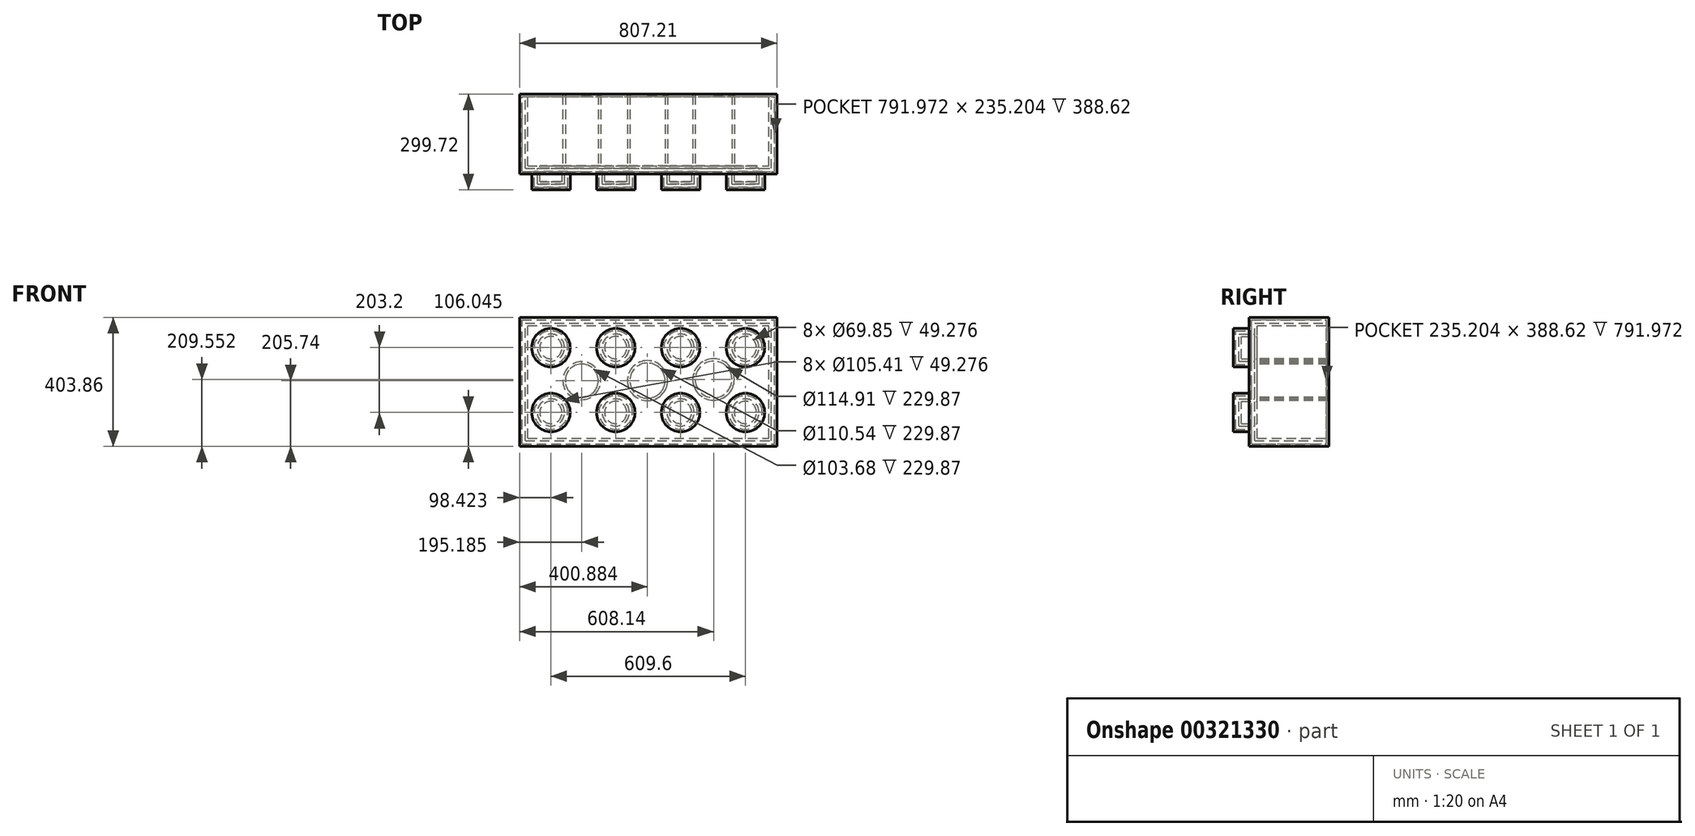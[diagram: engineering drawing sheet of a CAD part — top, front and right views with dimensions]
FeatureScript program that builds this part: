
annotation { "Feature Type Name" : "Feature", "Feature Type Description" : "" }
export const myFeature = defineFeature(function(context is Context, id is Id, definition is map)
    precondition{}
    {
        {
            var Q0;
            Q0=qCreatedBy(makeId("Front.planeOp"),FACE);
            var sketch = newSketch(context, id + "F0", { "sketchPlane" : qUnion([Q0])});
            skLineSegment(sketch, "E0.bottom", {"start": v(-361.72, 0) * mm, "end": v(445.49, 0) * mm});
            skLineSegment(sketch, "E0.top", {"start": v(-361.72, 403.86) * mm, "end": v(445.49, 403.86) * mm});
            skLineSegment(sketch, "E0.left", {"start": v(-361.72, 0) * mm, "end": v(-361.72, 403.86) * mm});
            skLineSegment(sketch, "E0.right", {"start": v(445.49, 0) * mm, "end": v(445.49, 403.86) * mm});
            skLineSegment(sketch, "E1.left", {"start": v(445.49, 0) * mm, "end": v(445.49, 0) * mm});
            skSolve(sketch);
        }
        {
            var Q0;
            Q0=makeQuery(id+"F0.imprint","IMPRINT",FACE,{"disambiguationData":[TD([[makeQuery(id+"F0.imprint","IMPRINT",EDGE,{"derivedFrom":sQuery(id+"F0.wireOp",EDGE,"E0.bottom")}),1.0]])]});
            extrude(context, id + "F1", {"entities" : qUnion([Q0]), "depth" : 250.44 * mm});
        }
        {
            var Q0;
            Q0=makeQuery(id+"F1.opExtrude","CAP_FACE",FACE,{"disambiguationData":[OSD([sQuery(id+"F0.wireOp",EDGE,"E0.bottom"),sQuery(id+"F0.wireOp",EDGE,"E0.top"),sQuery(id+"F0.wireOp",EDGE,"E0.left"),sQuery(id+"F0.wireOp",EDGE,"E0.right")])],"isStart":false});
            var sketch = newSketch(context, id + "F2", { "sketchPlane" : qUnion([Q0])});
            skCircle(sketch, "E2", {"center": v(-263.3, 309.25) * mm, "radius": 60.33 * mm});
            skCircle(sketch, "E3.0.1.0", {"center": v(-263.3, 106.05) * mm, "radius": 60.33 * mm});
            skCircle(sketch, "E3.1.0.0", {"center": v(-60.1, 309.25) * mm, "radius": 60.33 * mm});
            skCircle(sketch, "E3.1.1.0", {"center": v(-60.1, 106.05) * mm, "radius": 60.33 * mm});
            skCircle(sketch, "E3.2.0.0", {"center": v(143.1, 309.25) * mm, "radius": 60.33 * mm});
            skCircle(sketch, "E3.2.1.0", {"center": v(143.1, 106.05) * mm, "radius": 60.33 * mm});
            skCircle(sketch, "E3.3.0.0", {"center": v(346.3, 309.25) * mm, "radius": 60.33 * mm});
            skCircle(sketch, "E3.3.1.0", {"center": v(346.3, 106.05) * mm, "radius": 60.33 * mm});
            skLineSegment(sketch, "E3.direction1", {"start": v(-263.3, 309.25) * mm, "end": v(-60.1, 309.25) * mm, "construction": true});
            skLineSegment(sketch, "E3.direction2", {"start": v(-263.3, 309.25) * mm, "end": v(-263.3, 106.05) * mm, "construction": true});
            skSolve(sketch);
        }
        {
            var Q0;
            Q0 = qSketchRegion(id + "F2", true);
            extrude(context, id + "F3", {"entities" : qUnion([Q0]), "operationType" : NewBodyOperationType.ADD, "depth" : 49.28 * mm});
        }
        {
            var Q0;
            Q0=makeQuery(id+"F1.opExtrude","CAP_FACE",FACE,{"disambiguationData":[OSD([sQuery(id+"F0.wireOp",EDGE,"E0.bottom"),sQuery(id+"F0.wireOp",EDGE,"E0.top"),sQuery(id+"F0.wireOp",EDGE,"E0.left"),sQuery(id+"F0.wireOp",EDGE,"E0.right")])],"isStart":true});
            shell(context, id + "F4", {"entities" : qUnion([Q0]), "thickness" : 25.4 * mm});
        }
        {
            var Q0;
            Q0=makeQuery(id+"F4.opShell","OFFSET_FACE",FACE,{"disambiguationData":[OSD([sQuery(id+"F0.wireOp",EDGE,"E0.bottom"),sQuery(id+"F0.wireOp",EDGE,"E0.top"),sQuery(id+"F0.wireOp",EDGE,"E0.left"),sQuery(id+"F0.wireOp",EDGE,"E0.right")])]});
            var sketch = newSketch(context, id + "F5", { "sketchPlane" : qUnion([Q0])});
            skCircle(sketch, "E4", {"center": v(-246.42, 209.55) * mm, "radius": 65.08 * mm});
            skSolve(sketch);
        }
        {
            var Q0;
            Q0=makeQuery(id+"F5.imprint","IMPRINT",FACE,{"disambiguationData":[TD([[makeQuery(id+"F5.imprint","IMPRINT",EDGE,{"derivedFrom":sQuery(id+"F5.wireOp",EDGE,"E4")}),1.0]])]});
            extrude(context, id + "F6", {"entities" : qUnion([Q0]), "operationType" : NewBodyOperationType.ADD, "depth" : 222.25 * mm});
        }
        {
            var Q0;
            Q0=makeQuery(id+"F4.opShell","OFFSET_FACE",FACE,{"disambiguationData":[OSD([sQuery(id+"F0.wireOp",EDGE,"E0.bottom"),sQuery(id+"F0.wireOp",EDGE,"E0.top"),sQuery(id+"F0.wireOp",EDGE,"E0.left"),sQuery(id+"F0.wireOp",EDGE,"E0.right")])]});
            var sketch = newSketch(context, id + "F7", { "sketchPlane" : qUnion([Q0])});
            skCircle(sketch, "E5", {"center": v(-39.16, 205.74) * mm, "radius": 62.89 * mm});
            skSolve(sketch);
        }
        {
            var Q0;
            Q0=makeQuery(id+"F7.imprint","IMPRINT",FACE,{"disambiguationData":[TD([[makeQuery(id+"F7.imprint","IMPRINT",EDGE,{"derivedFrom":sQuery(id+"F7.wireOp",EDGE,"E5")}),1.0]])]});
            extrude(context, id + "F8", {"entities" : qUnion([Q0]), "operationType" : NewBodyOperationType.ADD, "depth" : 222.25 * mm});
        }
        {
            var Q0;
            Q0=makeQuery(id+"F4.opShell","OFFSET_FACE",FACE,{"disambiguationData":[OSD([sQuery(id+"F0.wireOp",EDGE,"E0.bottom"),sQuery(id+"F0.wireOp",EDGE,"E0.top"),sQuery(id+"F0.wireOp",EDGE,"E0.left"),sQuery(id+"F0.wireOp",EDGE,"E0.right")])]});
            var sketch = newSketch(context, id + "F9", { "sketchPlane" : qUnion([Q0])});
            skCircle(sketch, "E6", {"center": v(166.53, 205.74) * mm, "radius": 59.46 * mm});
            skSolve(sketch);
        }
        {
            var Q0;
            Q0=makeQuery(id+"F9.imprint","IMPRINT",FACE,{"disambiguationData":[TD([[makeQuery(id+"F9.imprint","IMPRINT",EDGE,{"derivedFrom":sQuery(id+"F9.wireOp",EDGE,"E6")}),1.0]])]});
            extrude(context, id + "F10", {"entities" : qUnion([Q0]), "operationType" : NewBodyOperationType.ADD, "depth" : 222.25 * mm});
        }
        {
            var Q0;
            Q0=makeQuery(id+"F6.opExtrude","CAP_FACE",FACE,{"disambiguationData":[OSD([sQuery(id+"F5.wireOp",EDGE,"E4")])],"isStart":false});
            var Q1;
            Q1=makeQuery(id+"F8.opExtrude","CAP_FACE",FACE,{"disambiguationData":[OSD([sQuery(id+"F7.wireOp",EDGE,"E5")])],"isStart":false});
            var Q2;
            Q2=makeQuery(id+"F10.opExtrude","CAP_FACE",FACE,{"disambiguationData":[OSD([sQuery(id+"F9.wireOp",EDGE,"E6")])],"isStart":false});
            shell(context, id + "F11", {"entities" : qUnion([Q0, Q1, Q2]), "thickness" : 7.62 * mm});
        }
    });
